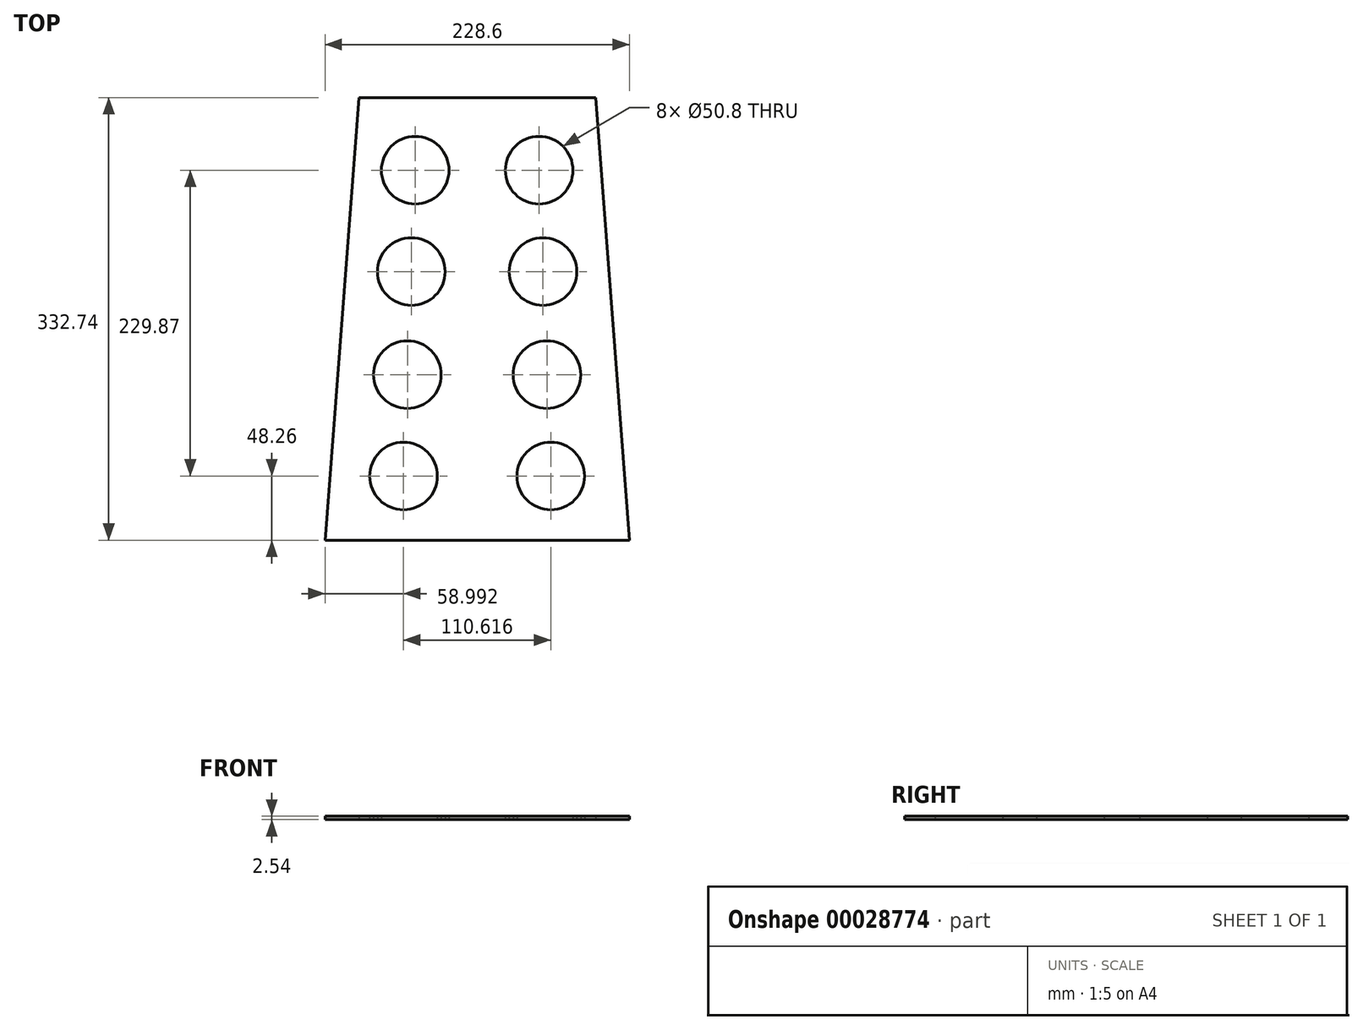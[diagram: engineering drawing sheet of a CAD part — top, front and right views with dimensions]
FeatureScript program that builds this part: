
annotation { "Feature Type Name" : "Feature", "Feature Type Description" : "" }
export const myFeature = defineFeature(function(context is Context, id is Id, definition is map)
    precondition{}
    {
        {
            var Q0;
            Q0=qCreatedBy(makeId("Top.planeOp"),FACE);
            var sketch = newSketch(context, id + "F0", { "sketchPlane" : qUnion([Q0])});
            skLineSegment(sketch, "E0.bottom", {"start": v(0, 0) * mm, "end": v(228.6, 0) * mm});
            skLineSegment(sketch, "E0.top", {"start": v(0, 332.74) * mm, "end": v(228.6, 332.74) * mm});
            skLineSegment(sketch, "E0.left", {"start": v(0, 0) * mm, "end": v(0, 332.74) * mm});
            skLineSegment(sketch, "E0.right", {"start": v(228.6, 0) * mm, "end": v(228.6, 332.74) * mm});
            skLineSegment(sketch, "E1", {"start": v(25.4, 332.74) * mm, "end": v(25.4, 0) * mm, "construction": true});
            skLineSegment(sketch, "E2", {"start": v(203.2, 332.74) * mm, "end": v(203.2, 0) * mm, "construction": true});
            skLineSegment(sketch, "E3", {"start": v(114.3, 332.74) * mm, "end": v(114.3, 0) * mm, "construction": true});
            skLineSegment(sketch, "E4", {"start": v(0, 0) * mm, "end": v(25.4, 332.74) * mm});
            skLineSegment(sketch, "E5", {"start": v(203.2, 332.74) * mm, "end": v(228.6, 0) * mm});
            skLineSegment(sketch, "E6", {"start": v(25.4, 332.74) * mm, "end": v(114.3, 332.74) * mm, "construction": true});
            skLineSegment(sketch, "E7", {"start": v(0, 0) * mm, "end": v(114.3, 0) * mm, "construction": true});
            skLineSegment(sketch, "E8", {"start": v(69.85, 332.74) * mm, "end": v(57.15, 0) * mm, "construction": true});
            skLineSegment(sketch, "E9", {"start": v(114.3, 332.74) * mm, "end": v(203.2, 332.74) * mm, "construction": true});
            skLineSegment(sketch, "E10", {"start": v(114.3, 0) * mm, "end": v(228.6, 0) * mm, "construction": true});
            skLineSegment(sketch, "E11", {"start": v(158.75, 332.74) * mm, "end": v(171.45, 0) * mm, "construction": true});
            skLineSegment(sketch, "E12", {"start": v(265.14, 332.74) * mm, "end": v(265.14, 0) * mm, "construction": true});
            skLineSegment(sketch, "E13", {"start": v(265.14, 0) * mm, "end": v(228.6, 0) * mm, "construction": true});
            skLineSegment(sketch, "E14", {"start": v(265.14, 48.26) * mm, "end": v(312.42, 48.26) * mm, "construction": true});
            skLineSegment(sketch, "E15", {"start": v(265.14, 124.46) * mm, "end": v(312.42, 124.46) * mm, "construction": true});
            skLineSegment(sketch, "E16", {"start": v(265.14, 201.93) * mm, "end": v(312.42, 201.93) * mm, "construction": true});
            skLineSegment(sketch, "E17", {"start": v(265.14, 278.13) * mm, "end": v(312.42, 278.13) * mm, "construction": true});
            skLineSegment(sketch, "E18", {"start": v(265.14, 278.13) * mm, "end": v(-83.9, 278.13) * mm, "construction": true});
            skLineSegment(sketch, "E19", {"start": v(265.14, 201.93) * mm, "end": v(-86.92, 201.93) * mm, "construction": true});
            skLineSegment(sketch, "E20", {"start": v(265.14, 124.46) * mm, "end": v(-82.9, 124.46) * mm, "construction": true});
            skLineSegment(sketch, "E21", {"start": v(265.14, 48.26) * mm, "end": v(-123.13, 48.26) * mm, "construction": true});
            skCircle(sketch, "E22", {"center": v(163.74, 201.93) * mm, "radius": 25.4 * mm});
            skCircle(sketch, "E23", {"center": v(166.7, 124.46) * mm, "radius": 25.4 * mm});
            skCircle(sketch, "E24", {"center": v(169.6, 48.26) * mm, "radius": 25.4 * mm});
            skCircle(sketch, "E25", {"center": v(59, 48.26) * mm, "radius": 25.4 * mm});
            skCircle(sketch, "E26", {"center": v(61.9, 124.46) * mm, "radius": 25.4 * mm});
            skCircle(sketch, "E27", {"center": v(64.86, 201.93) * mm, "radius": 25.4 * mm});
            skCircle(sketch, "E28", {"center": v(67.77, 278.13) * mm, "radius": 25.4 * mm});
            skCircle(sketch, "E29", {"center": v(160.83, 278.13) * mm, "radius": 25.4 * mm});
            skSolve(sketch);
        }
        {
            var Q0;
            Q0=makeQuery(id+"F0.imprint","IMPRINT",FACE,{"disambiguationData":[TD([[makeQuery(id+"F0.imprint","IMPRINT",EDGE,{"derivedFrom":sQuery(id+"F0.wireOp",EDGE,"E0.bottom")}),1.0]])]});
            extrude(context, id + "F1", {"entities" : qUnion([Q0]), "depth" : 2.54 * mm});
        }
    });
